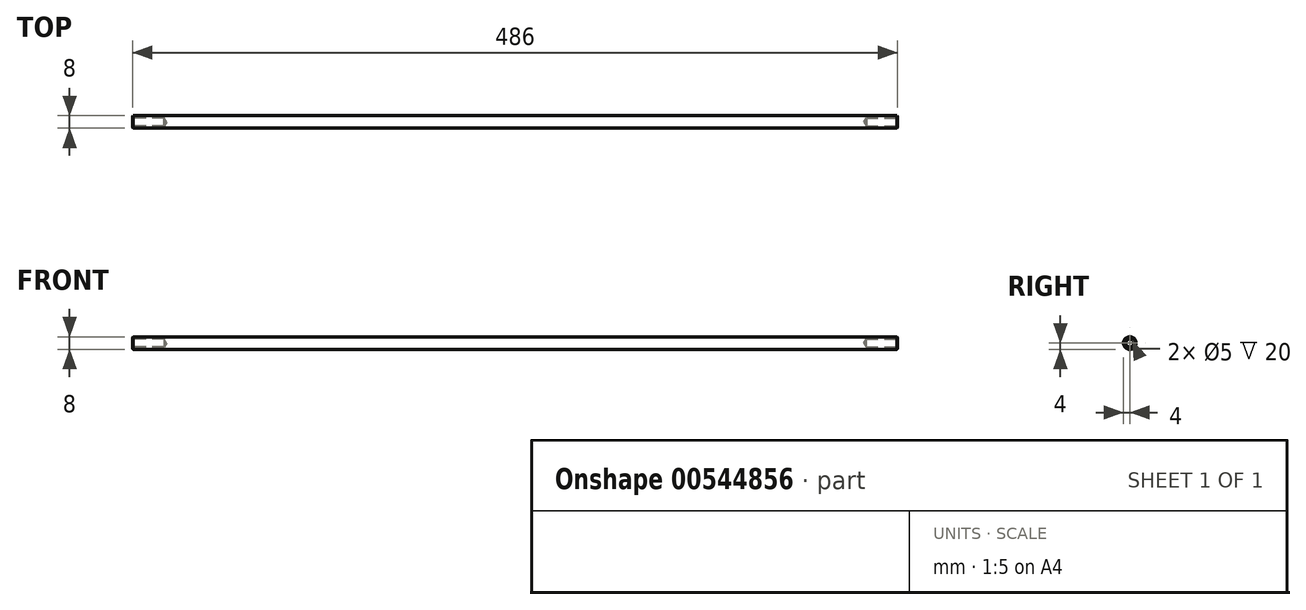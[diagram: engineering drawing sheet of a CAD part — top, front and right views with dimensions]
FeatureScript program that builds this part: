
annotation { "Feature Type Name" : "Feature", "Feature Type Description" : "" }
export const myFeature = defineFeature(function(context is Context, id is Id, definition is map)
    precondition{}
    {
        {
            var Q0;
            Q0=qCreatedBy(makeId("Right.planeOp"),FACE);
            var sketch = newSketch(context, id + "F0", { "sketchPlane" : qUnion([Q0])});
            skCircle(sketch, "E0", {"center": v(0, 0) * mm, "radius": 4 * mm});
            skSolve(sketch);
        }
        {
            var Q0;
            Q0 = qSketchRegion(id + "F0", true);
            extrude(context, id + "F1", {"entities" : qUnion([Q0]), "depth" : 486 * mm, "offsetDistance" : 25 * mm});
        }
        {
            var Q0;
            Q0=makeQuery(id+"F1.opExtrude","CAP_FACE",FACE,{"disambiguationData":[OSD([sQuery(id+"F0.wireOp",EDGE,"E0")])],"isStart":false});
            var sketch = newSketch(context, id + "F2", { "sketchPlane" : qUnion([Q0])});
            skCircle(sketch, "E1", {"center": v(0, 0) * mm, "radius": 6.43 * mm});
            skSolve(sketch);
        }
        {
            var Q0;
            Q0=makeQuery(id+"F1.opExtrude","CAP_FACE",FACE,{"disambiguationData":[OSD([sQuery(id+"F0.wireOp",EDGE,"E0")])],"isStart":true});
            var sketch = newSketch(context, id + "F3", { "sketchPlane" : qUnion([Q0])});
            skCircle(sketch, "E2", {"center": v(0, 0) * mm, "radius": 10.6 * mm});
            skSolve(sketch);
        }
        {
            var Q0;
            Q0=sQuery(id+"F3.wireOp",VERTEX,"E2.center");
            var Q1;
            Q1=sQuery(id+"F2.wireOp",VERTEX,"E1.center");
            var Q2;
            Q2=makeQuery(id+"F1.opExtrude","SWEPT_BODY",BODY,{"disambiguationData":[OSD([sQuery(id+"F0.wireOp",EDGE,"E0")])]});
            hole(context, id + "F4", {"style" : HoleStyle.SIMPLE, "endStyle" : HoleEndStyle.BLIND, "holeDiameter" : 5 * mm, "holeDepth" : 20 * mm, "isTappedThrough" : true, "tappedDepth" : 12 * mm, "tapClearance" : 3, "locations" : qUnion([Q0, Q1]), "scope" : qUnion([Q2])});
        }
        {
            var Q0;
            Q0=makeQuery(id+"F1.opExtrude","CAP_EDGE",EDGE,{"disambiguationData":[OSD([sQuery(id+"F0.wireOp",EDGE,"E0")])],"isStart":false});
            var Q1;
            Q1=makeQuery(id+"F1.opExtrude","CAP_EDGE",EDGE,{"disambiguationData":[OSD([sQuery(id+"F0.wireOp",EDGE,"E0")])],"isStart":true});
            chamfer(context, id + "F5", {"entities" : qUnion([Q0, Q1]), "width" : 0.5 * mm, "tangentPropagation" : true});
        }
    });
